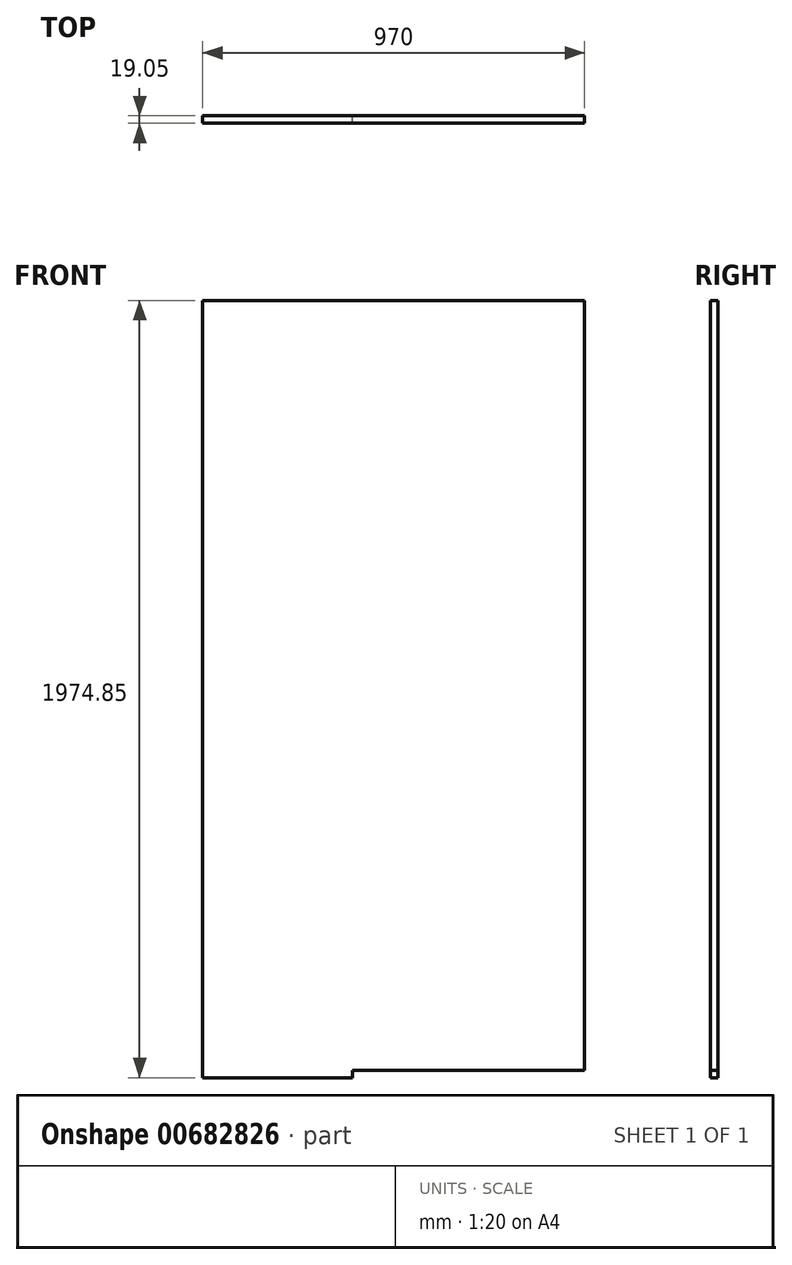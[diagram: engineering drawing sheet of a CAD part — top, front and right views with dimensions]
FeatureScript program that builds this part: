
annotation { "Feature Type Name" : "Feature", "Feature Type Description" : "" }
export const myFeature = defineFeature(function(context is Context, id is Id, definition is map)
    precondition{}
    {
        {
            var Q0;
            Q0=qCreatedBy(makeId("Front.planeOp"),FACE);
            var sketch = newSketch(context, id + "F0", { "sketchPlane" : qUnion([Q0])});
            skLineSegment(sketch, "E0.bottom", {"start": v(0, 0) * mm, "end": v(-589, 0) * mm});
            skLineSegment(sketch, "E0.left", {"start": v(0, 0) * mm, "end": v(0, 1955.8) * mm});
            skLineSegment(sketch, "E0.right", {"start": v(-970, -19.05) * mm, "end": v(-970, 1955.8) * mm});
            skLineSegment(sketch, "E1", {"start": v(0, 1955.8) * mm, "end": v(-970, 1955.8) * mm});
            skLineSegment(sketch, "E2", {"start": v(-970, -19.05) * mm, "end": v(-589, -19.05) * mm});
            skLineSegment(sketch, "E3", {"start": v(-589, 0) * mm, "end": v(-589, -19.05) * mm});
            skSolve(sketch);
        }
        {
            var Q0;
            Q0=qSketchRegion(id+"F0",true);
            extrude(context, id + "F1", {"entities" : qUnion([Q0]), "depth" : 19.05 * mm, "offsetDistance" : 25.4 * mm});
        }
    });
